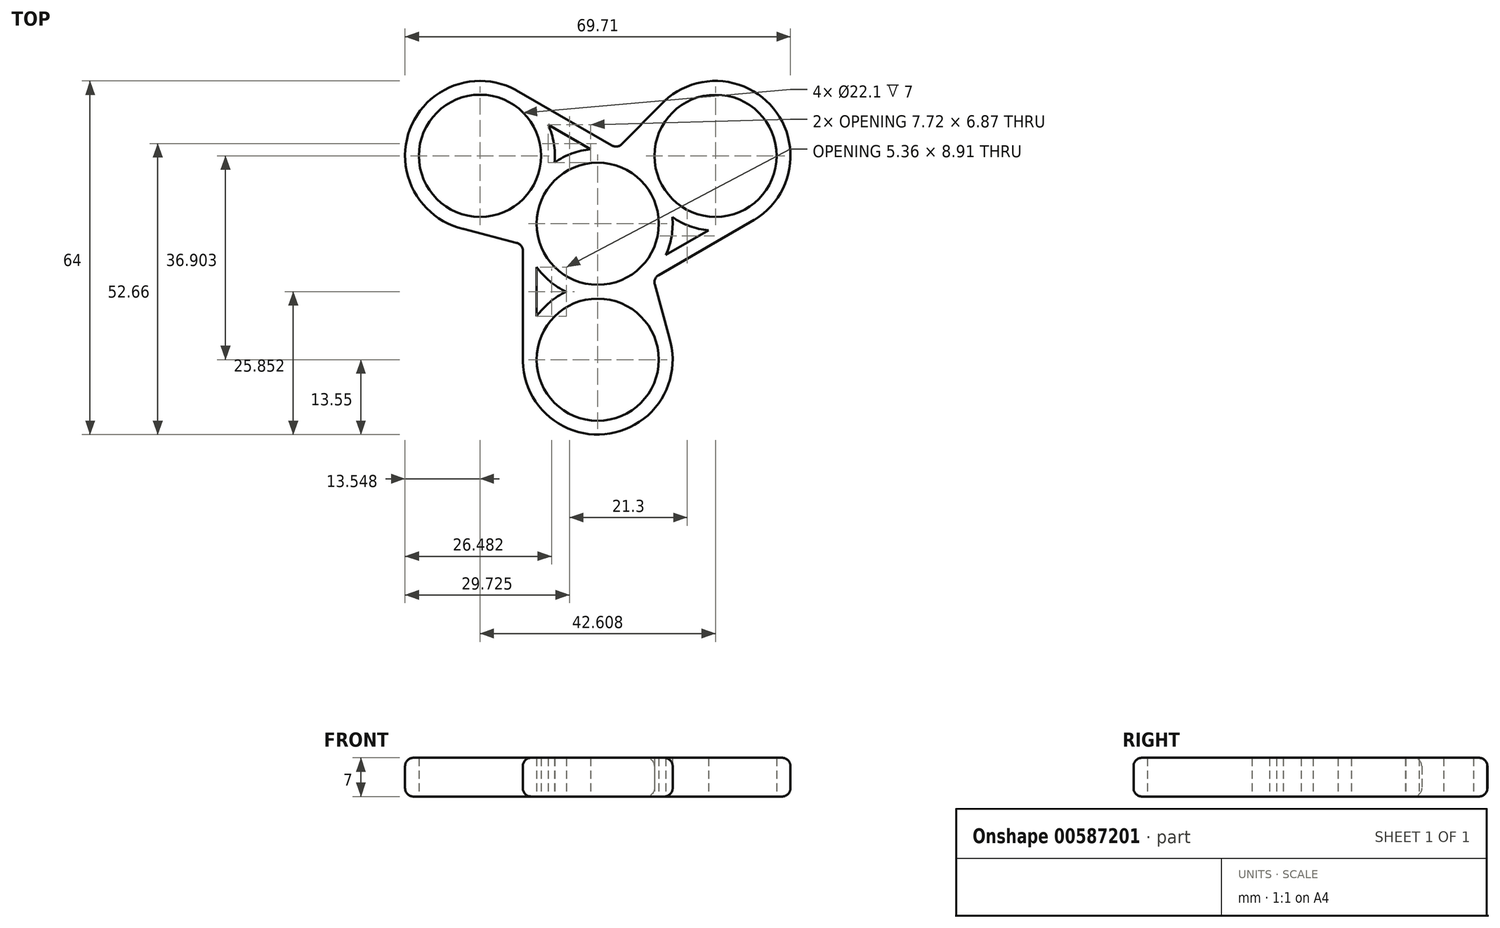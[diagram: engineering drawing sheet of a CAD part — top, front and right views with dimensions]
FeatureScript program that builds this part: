
annotation { "Feature Type Name" : "Feature", "Feature Type Description" : "" }
export const myFeature = defineFeature(function(context is Context, id is Id, definition is map)
    precondition{}
    {
        {
            var Q0;
            Q0=qCreatedBy(makeId("Top.planeOp"),FACE);
            var sketch = newSketch(context, id + "F0", { "sketchPlane" : qUnion([Q0])});
            skCircle(sketch, "E0", {"center": v(0, 0) * mm, "radius": 11.05 * mm});
            skCircle(sketch, "E1", {"center": v(0, -24.6) * mm, "radius": 11.05 * mm});
            skCircle(sketch, "E2.0", {"center": v(0, -24.6) * mm, "radius": 13.55 * mm});
            skLineSegment(sketch, "E3.bottom", {"start": v(-13.55, 0) * mm, "end": v(7.31, 0) * mm});
            skLineSegment(sketch, "E3.left", {"start": v(-13.55, 0) * mm, "end": v(-13.55, -24.9) * mm});
            skLineSegment(sketch, "E3.right", {"start": v(7.31, 0) * mm, "end": v(12.94, -20.58) * mm});
            skCircle(sketch, "E4.0", {"center": v(0, 0) * mm, "radius": 13.55 * mm});
            skLineSegment(sketch, "E5", {"start": v(-11.05, -7.84) * mm, "end": v(-11.05, -16.75) * mm});
            skLineSegment(sketch, "E6.1.0", {"start": v(-3.66, 6.33) * mm, "end": v(11.36, 21.5) * mm});
            skCircle(sketch, "E6.1.1", {"center": v(21.3, 12.3) * mm, "radius": 13.55 * mm});
            skCircle(sketch, "E6.1.2", {"center": v(21.3, 12.3) * mm, "radius": 11.05 * mm});
            skLineSegment(sketch, "E6.1.3", {"start": v(12.32, -5.65) * mm, "end": v(20.03, -1.2) * mm});
            skLineSegment(sketch, "E6.1.4", {"start": v(6.78, -11.73) * mm, "end": v(28.34, 0.72) * mm});
            skLineSegment(sketch, "E6.1.5", {"start": v(6.78, -11.73) * mm, "end": v(-3.66, 6.33) * mm});
            skLineSegment(sketch, "E6.2.0", {"start": v(-3.66, -6.33) * mm, "end": v(-24.3, -0.91) * mm});
            skCircle(sketch, "E6.2.1", {"center": v(-21.3, 12.3) * mm, "radius": 13.55 * mm});
            skCircle(sketch, "E6.2.2", {"center": v(-21.3, 12.3) * mm, "radius": 11.05 * mm});
            skLineSegment(sketch, "E6.2.3", {"start": v(-1.27, 13.5) * mm, "end": v(-8.98, 17.95) * mm});
            skLineSegment(sketch, "E6.2.4", {"start": v(6.77, 11.73) * mm, "end": v(-14.8, 24.19) * mm});
            skLineSegment(sketch, "E6.2.5", {"start": v(6.78, 11.73) * mm, "end": v(-3.66, -6.33) * mm});
            skSolve(sketch);
        }
        {
            var Q0;
            {var subQ3=sQuery(id+"F0.wireOp",EDGE,"E6.2.0");var subQ5=sQuery(id+"F0.wireOp",EDGE,"E6.2.1");var subQ7=makeQuery(id+"F0.imprint","INTERSECT",VERTEX,{"derivedFrom":[subQ3,subQ5]});Q0=makeQuery(id+"F0.imprint","IMPRINT",FACE,{"disambiguationData":[TD([[makeQuery(id+"F0.imprint","IMPRINT",EDGE,{"disambiguationData":[TD([[subQ7,1.0]])],"derivedFrom":subQ3}),-1.0]])]});}
            var Q1;
            {var subQ7=sQuery(id+"F0.wireOp",EDGE,"E6.2.2");Q1=makeQuery(id+"F0.imprint","IMPRINT",FACE,{"disambiguationData":[TD([[makeQuery(id+"F0.imprint","IMPRINT",EDGE,{"derivedFrom":subQ7}),-1.0]])]});}
            var Q2;
            {var subQ0=sQuery(id+"F0.wireOp",EDGE,"E4.0");var subQ1=makeQuery(id+"F0.imprint","INTERSECT",VERTEX,{"derivedFrom":[subQ0,sQuery(id+"F0.wireOp",EDGE,"E6.2.2")]});Q2=makeQuery(id+"F0.imprint","IMPRINT",FACE,{"disambiguationData":[TD([[makeQuery(id+"F0.imprint","IMPRINT",EDGE,{"disambiguationData":[TD([[subQ1,1.0]])],"derivedFrom":subQ0}),1.0]])]});}
            var Q3;
            {var subQ0=sQuery(id+"F0.wireOp",EDGE,"E6.2.1");var subQ1=sQuery(id+"F0.wireOp",EDGE,"E0");var subQ2=makeQuery(id+"F0.imprint","INTERSECT",VERTEX,{"derivedFrom":[subQ1,subQ0]});Q3=makeQuery(id+"F0.imprint","IMPRINT",FACE,{"disambiguationData":[TD([[makeQuery(id+"F0.imprint","IMPRINT",EDGE,{"disambiguationData":[TD([[subQ2,-1.0]])],"derivedFrom":subQ1}),-1.0]])]});}
            var Q4;
            {var subQ0=sQuery(id+"F0.wireOp",EDGE,"E3.bottom");var subQ1=sQuery(id+"F0.wireOp",EDGE,"E0");var subQ2=makeQuery(id+"F0.imprint","INTERSECT",VERTEX,{"derivedFrom":[subQ1,subQ0]});Q4=makeQuery(id+"F0.imprint","IMPRINT",FACE,{"disambiguationData":[TD([[makeQuery(id+"F0.imprint","IMPRINT",EDGE,{"disambiguationData":[TD([[subQ2,-1.0]])],"derivedFrom":subQ1}),-1.0]])]});}
            var Q5;
            {var subQ2=sQuery(id+"F0.wireOp",EDGE,"E6.2.0");var subQ6=sQuery(id+"F0.wireOp",EDGE,"E0");var subQ7=makeQuery(id+"F0.imprint","INTERSECT",VERTEX,{"derivedFrom":[subQ6,subQ2]});Q5=makeQuery(id+"F0.imprint","IMPRINT",FACE,{"disambiguationData":[TD([[makeQuery(id+"F0.imprint","IMPRINT",EDGE,{"disambiguationData":[TD([[subQ7,-1.0]])],"derivedFrom":subQ6}),-1.0]])]});}
            var Q6;
            {var subQ0=sQuery(id+"F0.wireOp",EDGE,"E5");Q6=makeQuery(id+"F0.imprint","IMPRINT",FACE,{"disambiguationData":[TD([[makeQuery(id+"F0.imprint","IMPRINT",EDGE,{"derivedFrom":subQ0}),-1.0]])]});}
            var Q7;
            {var subQ9=sQuery(id+"F0.wireOp",EDGE,"E1");Q7=makeQuery(id+"F0.imprint","IMPRINT",FACE,{"disambiguationData":[TD([[makeQuery(id+"F0.imprint","IMPRINT",EDGE,{"derivedFrom":subQ9}),-1.0]])]});}
            var Q8;
            {var subQ0=sQuery(id+"F0.wireOp",EDGE,"E2.0");var subQ1=makeQuery(id+"F0.imprint","INTERSECT",VERTEX,{"derivedFrom":[sQuery(id+"F0.wireOp",EDGE,"E0"),subQ0]});Q8=makeQuery(id+"F0.imprint","IMPRINT",FACE,{"disambiguationData":[TD([[makeQuery(id+"F0.imprint","IMPRINT",EDGE,{"disambiguationData":[TD([[subQ1,1.0]])],"derivedFrom":subQ0}),1.0]])]});}
            var Q9;
            {var subQ0=sQuery(id+"F0.wireOp",EDGE,"E2.0");var subQ1=sQuery(id+"F0.wireOp",EDGE,"E0");var subQ2=makeQuery(id+"F0.imprint","INTERSECT",VERTEX,{"derivedFrom":[subQ1,subQ0]});Q9=makeQuery(id+"F0.imprint","IMPRINT",FACE,{"disambiguationData":[TD([[makeQuery(id+"F0.imprint","IMPRINT",EDGE,{"disambiguationData":[TD([[subQ2,-1.0]])],"derivedFrom":subQ1}),-1.0]])]});}
            var Q10;
            {var subQ0=sQuery(id+"F0.wireOp",EDGE,"E6.1.5");var subQ1=sQuery(id+"F0.wireOp",EDGE,"E0");var subQ2=makeQuery(id+"F0.imprint","INTERSECT",VERTEX,{"derivedFrom":[subQ1,subQ0]});Q10=makeQuery(id+"F0.imprint","IMPRINT",FACE,{"disambiguationData":[TD([[makeQuery(id+"F0.imprint","IMPRINT",EDGE,{"disambiguationData":[TD([[subQ2,-1.0]])],"derivedFrom":subQ1}),-1.0]])]});}
            var Q11;
            {var subQ2=sQuery(id+"F0.wireOp",EDGE,"E6.1.1");var subQ5=sQuery(id+"F0.wireOp",EDGE,"E0");var subQ8=makeQuery(id+"F0.imprint","INTERSECT",VERTEX,{"derivedFrom":[subQ5,subQ2]});Q11=makeQuery(id+"F0.imprint","IMPRINT",FACE,{"disambiguationData":[TD([[makeQuery(id+"F0.imprint","IMPRINT",EDGE,{"disambiguationData":[TD([[subQ8,1.0]])],"derivedFrom":subQ5}),-1.0]])]});}
            var Q12;
            {var subQ0=sQuery(id+"F0.wireOp",EDGE,"E6.1.3");Q12=makeQuery(id+"F0.imprint","IMPRINT",FACE,{"disambiguationData":[TD([[makeQuery(id+"F0.imprint","IMPRINT",EDGE,{"derivedFrom":subQ0}),-1.0]])]});}
            var Q13;
            {var subQ6=sQuery(id+"F0.wireOp",EDGE,"E6.1.2");Q13=makeQuery(id+"F0.imprint","IMPRINT",FACE,{"disambiguationData":[TD([[makeQuery(id+"F0.imprint","IMPRINT",EDGE,{"derivedFrom":subQ6}),-1.0]])]});}
            var Q14;
            {var subQ0=sQuery(id+"F0.wireOp",EDGE,"E4.0");var subQ1=makeQuery(id+"F0.imprint","INTERSECT",VERTEX,{"derivedFrom":[subQ0,sQuery(id+"F0.wireOp",EDGE,"E6.1.2")]});Q14=makeQuery(id+"F0.imprint","IMPRINT",FACE,{"disambiguationData":[TD([[makeQuery(id+"F0.imprint","IMPRINT",EDGE,{"disambiguationData":[TD([[subQ1,1.0]])],"derivedFrom":subQ0}),1.0]])]});}
            var Q15;
            {var subQ3=sQuery(id+"F0.wireOp",EDGE,"E6.1.1");var subQ5=sQuery(id+"F0.wireOp",EDGE,"E6.1.0");var subQ6=makeQuery(id+"F0.imprint","INTERSECT",VERTEX,{"derivedFrom":[subQ5,subQ3]});Q15=makeQuery(id+"F0.imprint","IMPRINT",FACE,{"disambiguationData":[TD([[makeQuery(id+"F0.imprint","IMPRINT",EDGE,{"disambiguationData":[TD([[subQ6,1.0]])],"derivedFrom":subQ5}),-1.0]])]});}
            var Q16;
            {var subQ0=sQuery(id+"F0.wireOp",EDGE,"E6.2.3");Q16=makeQuery(id+"F0.imprint","IMPRINT",FACE,{"disambiguationData":[TD([[makeQuery(id+"F0.imprint","IMPRINT",EDGE,{"derivedFrom":subQ0}),-1.0]])]});}
            var Q17;
            {var subQ2=sQuery(id+"F0.wireOp",EDGE,"E6.1.0");var subQ4=sQuery(id+"F0.wireOp",EDGE,"E0");var subQ5=makeQuery(id+"F0.imprint","INTERSECT",VERTEX,{"derivedFrom":[subQ4,subQ2]});Q17=makeQuery(id+"F0.imprint","IMPRINT",FACE,{"disambiguationData":[TD([[makeQuery(id+"F0.imprint","IMPRINT",EDGE,{"disambiguationData":[TD([[subQ5,-1.0]])],"derivedFrom":subQ4}),-1.0]])]});}
            var Q18;
            {var subQ0=sQuery(id+"F0.wireOp",EDGE,"E6.2.5");var subQ1=sQuery(id+"F0.wireOp",EDGE,"E0");var subQ2=makeQuery(id+"F0.imprint","INTERSECT",VERTEX,{"derivedFrom":[subQ1,subQ0]});Q18=makeQuery(id+"F0.imprint","IMPRINT",FACE,{"disambiguationData":[TD([[makeQuery(id+"F0.imprint","IMPRINT",EDGE,{"disambiguationData":[TD([[subQ2,-1.0]])],"derivedFrom":subQ1}),-1.0]])]});}
            var Q19;
            {var subQ0=sQuery(id+"F0.wireOp",EDGE,"E6.2.5");var subQ1=sQuery(id+"F0.wireOp",EDGE,"E0");var subQ2=makeQuery(id+"F0.imprint","INTERSECT",VERTEX,{"derivedFrom":[subQ1,subQ0]});Q19=makeQuery(id+"F0.imprint","IMPRINT",FACE,{"disambiguationData":[TD([[makeQuery(id+"F0.imprint","IMPRINT",EDGE,{"disambiguationData":[TD([[subQ2,1.0]])],"derivedFrom":subQ1}),-1.0]])]});}
            var Q20;
            {var subQ0=sQuery(id+"F0.wireOp",EDGE,"E6.2.4");var subQ3=sQuery(id+"F0.wireOp",EDGE,"E6.1.0");var subQ5=makeQuery(id+"F0.imprint","INTERSECT",VERTEX,{"derivedFrom":[subQ3,subQ0]});Q20=makeQuery(id+"F0.imprint","IMPRINT",FACE,{"disambiguationData":[TD([[makeQuery(id+"F0.imprint","IMPRINT",EDGE,{"disambiguationData":[TD([[subQ5,1.0]])],"derivedFrom":subQ3}),-1.0]])]});}
            var Q21;
            {var subQ1=sQuery(id+"F0.wireOp",EDGE,"E3.left");var subQ3=sQuery(id+"F0.wireOp",EDGE,"E6.2.0");var subQ4=makeQuery(id+"F0.imprint","INTERSECT",VERTEX,{"derivedFrom":[subQ1,subQ3]});Q21=makeQuery(id+"F0.imprint","IMPRINT",FACE,{"disambiguationData":[TD([[makeQuery(id+"F0.imprint","IMPRINT",EDGE,{"disambiguationData":[TD([[subQ4,1.0]])],"derivedFrom":subQ3}),-1.0]])]});}
            var Q22;
            {var subQ0=sQuery(id+"F0.wireOp",EDGE,"E6.1.4");var subQ1=sQuery(id+"F0.wireOp",EDGE,"E3.right");var subQ2=makeQuery(id+"F0.imprint","INTERSECT",VERTEX,{"derivedFrom":[subQ1,subQ0]});Q22=makeQuery(id+"F0.imprint","IMPRINT",FACE,{"disambiguationData":[TD([[makeQuery(id+"F0.imprint","IMPRINT",EDGE,{"disambiguationData":[TD([[subQ2,1.0]])],"derivedFrom":subQ1}),-1.0]])]});}
            var Q23;
            {var subQ0=sQuery(id+"F0.wireOp",EDGE,"E3.right");var subQ1=sQuery(id+"F0.wireOp",EDGE,"E2.0");var subQ2=makeQuery(id+"F0.imprint","INTERSECT",VERTEX,{"derivedFrom":[subQ1,subQ0]});Q23=makeQuery(id+"F0.imprint","IMPRINT",FACE,{"disambiguationData":[TD([[makeQuery(id+"F0.imprint","IMPRINT",EDGE,{"disambiguationData":[TD([[subQ2,-1.0]])],"derivedFrom":subQ1}),-1.0]])]});}
            extrude(context, id + "F1", {"entities" : qUnion([Q0, Q1, Q2, Q3, Q4, Q5, Q6, Q7, Q8, Q9, Q10, Q11, Q12, Q13, Q14, Q15, Q16, Q17, Q18, Q19, Q20, Q21, Q22, Q23]), "depth" : 7 * mm, "offsetDistance" : 25 * mm});
        }
        {
            var Q0;
            {var subQ0=sQuery(id+"F0.wireOp",EDGE,"E2.0");Q0=makeQuery(id+"F1.opExtrude","SWEPT_FACE",FACE,{"disambiguationData":[OSD([subQ0]),TDD([makeQuery(id+"F0.imprint","IMPRINT",EDGE,{"disambiguationData":[TD([[makeQuery(id+"F0.imprint","INTERSECT",VERTEX,{"disambiguationData":[OD(0.0)],"derivedFrom":[subQ0,sQuery(id+"F0.wireOp",EDGE,"E3.left")]}),-1.0]])],"derivedFrom":subQ0})])]});}
            var Q1;
            Q1=makeQuery(id+"F1.opExtrude","SWEPT_FACE",FACE,{"disambiguationData":[OSD([sQuery(id+"F0.wireOp",EDGE,"E3.right")])]});
            var Q2;
            Q2=makeQuery(id+"F1.opExtrude","SWEPT_FACE",FACE,{"disambiguationData":[OSD([sQuery(id+"F0.wireOp",EDGE,"E6.1.4")])]});
            var Q3;
            {var subQ0=sQuery(id+"F0.wireOp",EDGE,"E6.1.1");Q3=makeQuery(id+"F1.opExtrude","SWEPT_FACE",FACE,{"disambiguationData":[OSD([subQ0]),TDD([makeQuery(id+"F0.imprint","IMPRINT",EDGE,{"disambiguationData":[TD([[makeQuery(id+"F0.imprint","INTERSECT",VERTEX,{"derivedFrom":[sQuery(id+"F0.wireOp",EDGE,"E6.1.0"),subQ0]}),1.0]])],"derivedFrom":subQ0})])]});}
            var Q4;
            Q4=makeQuery(id+"F1.opExtrude","SWEPT_FACE",FACE,{"disambiguationData":[OSD([sQuery(id+"F0.wireOp",EDGE,"E6.1.0")])]});
            var Q5;
            Q5=makeQuery(id+"F1.opExtrude","SWEPT_FACE",FACE,{"disambiguationData":[OSD([sQuery(id+"F0.wireOp",EDGE,"E6.2.4")])]});
            var Q6;
            {var subQ0=sQuery(id+"F0.wireOp",EDGE,"E6.2.1");Q6=makeQuery(id+"F1.opExtrude","SWEPT_FACE",FACE,{"disambiguationData":[OSD([subQ0]),TDD([makeQuery(id+"F0.imprint","IMPRINT",EDGE,{"disambiguationData":[TD([[makeQuery(id+"F0.imprint","INTERSECT",VERTEX,{"derivedFrom":[sQuery(id+"F0.wireOp",EDGE,"E6.2.0"),subQ0]}),1.0]])],"derivedFrom":subQ0})])]});}
            var Q7;
            Q7=makeQuery(id+"F1.opExtrude","SWEPT_FACE",FACE,{"disambiguationData":[OSD([sQuery(id+"F0.wireOp",EDGE,"E6.2.0")])]});
            var Q8;
            Q8=makeQuery(id+"F1.opExtrude","SWEPT_FACE",FACE,{"disambiguationData":[OSD([sQuery(id+"F0.wireOp",EDGE,"E3.left")])]});
            fillet(context, id + "F2", {"entities" : qUnion([Q0, Q1, Q2, Q3, Q4, Q5, Q6, Q7, Q8]), "radius" : 1.5 * mm, "tangentPropagation" : true, "allowEdgeOverflow" : false});
        }
    });
